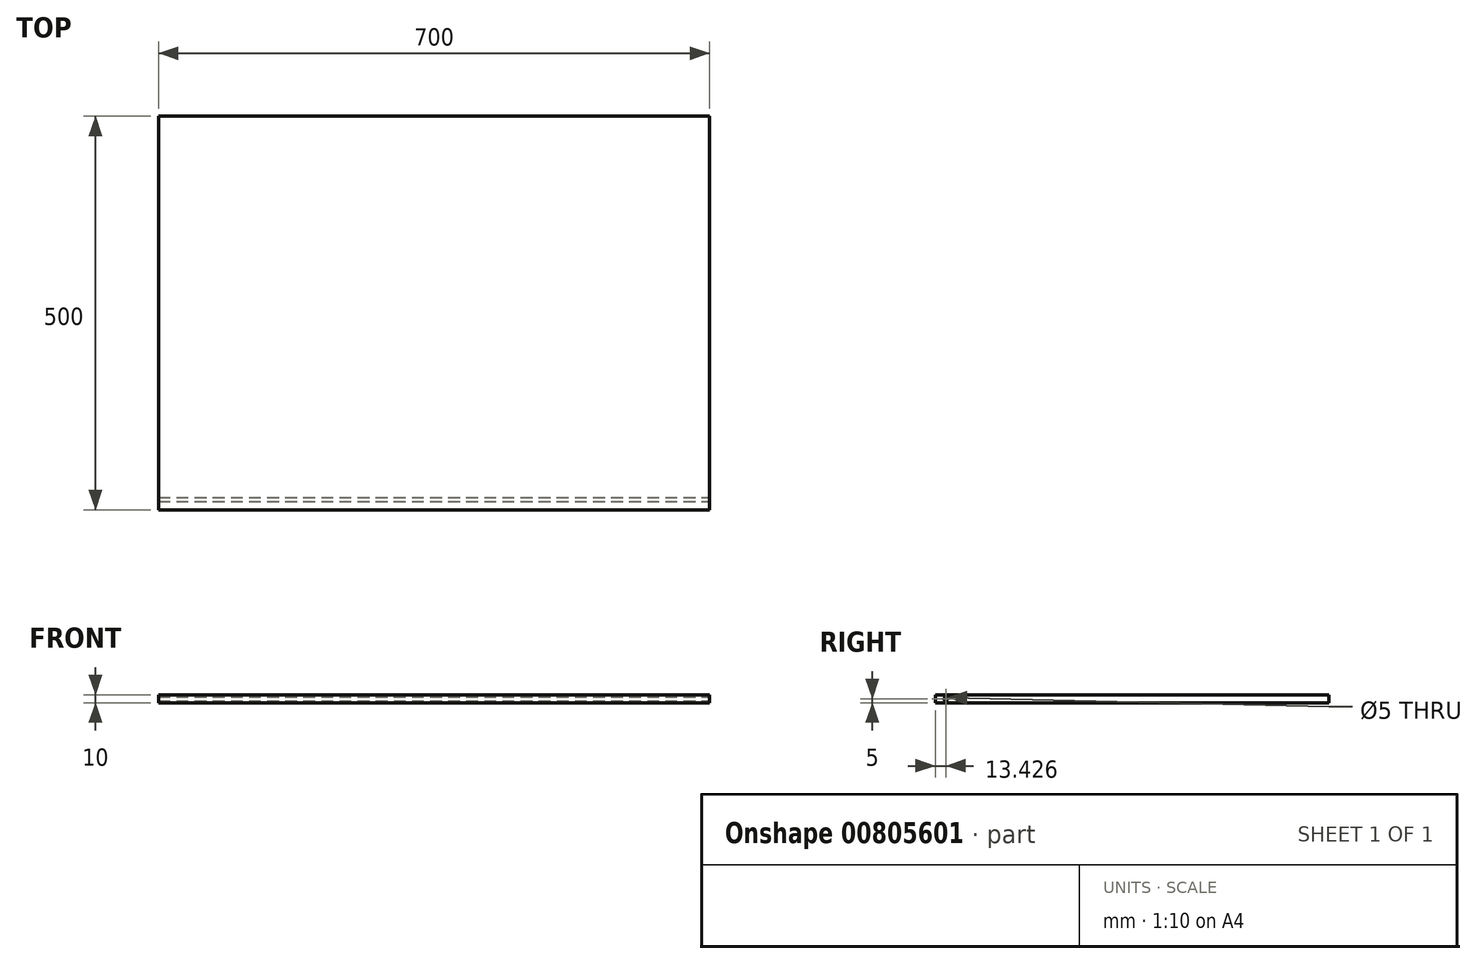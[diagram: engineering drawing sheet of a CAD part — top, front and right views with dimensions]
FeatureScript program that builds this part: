
annotation { "Feature Type Name" : "Feature", "Feature Type Description" : "" }
export const myFeature = defineFeature(function(context is Context, id is Id, definition is map)
    precondition{}
    {
        {
            var Q0;
            Q0=qCreatedBy(makeId("Top.planeOp"),FACE);
            var sketch = newSketch(context, id + "F0", { "sketchPlane" : qUnion([Q0])});
            skLineSegment(sketch, "E0.bottom", {"start": v(-346.8, 224.54) * mm, "end": v(353.2, 224.54) * mm});
            skLineSegment(sketch, "E0.top", {"start": v(-346.8, -275.46) * mm, "end": v(353.2, -275.46) * mm});
            skLineSegment(sketch, "E0.left", {"start": v(-346.8, 224.54) * mm, "end": v(-346.8, -275.46) * mm});
            skLineSegment(sketch, "E0.right", {"start": v(353.2, 224.54) * mm, "end": v(353.2, -275.46) * mm});
            skSolve(sketch);
        }
        {
            var Q0;
            Q0 = qSketchRegion(id + "F0", true);
            extrude(context, id + "F1", {"entities" : qUnion([Q0]), "depth" : 10 * mm, "offsetDistance" : 25 * mm});
        }
        {
            var Q0;
            Q0=makeQuery(id+"F1.opExtrude","SWEPT_FACE",FACE,{"disambiguationData":[OSD([sQuery(id+"F0.wireOp",EDGE,"E0.right")])]});
            var sketch = newSketch(context, id + "F2", { "sketchPlane" : qUnion([Q0])});
            skCircle(sketch, "E1", {"center": v(-266.18, 5.85) * mm, "radius": 4.15 * mm});
            skSolve(sketch);
        }
        {
            var Q0;
            Q0 = qSketchRegion(id + "F2", true);
            extrude(context, id + "F3", {"entities" : qUnion([Q0]), "operationType" : NewBodyOperationType.ADD, "oppositeDirection" : true, "depth" : 700 * mm, "offsetDistance" : 25 * mm});
        }
        {
            var Q0;
            Q0=makeQuery(id+"F1.opExtrude","SWEPT_FACE",FACE,{"disambiguationData":[OSD([sQuery(id+"F0.wireOp",EDGE,"E0.right")])]});
            var sketch = newSketch(context, id + "F4", { "sketchPlane" : qUnion([Q0])});
            skCircle(sketch, "E2", {"center": v(-262.03, 5) * mm, "radius": 3.78 * mm});
            skPoint(sketch, "E2.centerSnap0", {"position": v(-275.46, 5) * mm});
            skSolve(sketch);
        }
        {
            var Q0;
            Q0=sQuery(id+"F4.wireOp",VERTEX,"E2.center");
            var Q1;
            Q1=makeQuery(id+"F1.opExtrude","SWEPT_BODY",BODY,{"disambiguationData":[OSD([sQuery(id+"F0.wireOp",EDGE,"E0.bottom"),sQuery(id+"F0.wireOp",EDGE,"E0.top"),sQuery(id+"F0.wireOp",EDGE,"E0.left"),sQuery(id+"F0.wireOp",EDGE,"E0.right")])]});
            hole(context, id + "F5", {"style" : HoleStyle.SIMPLE, "endStyle" : HoleEndStyle.THROUGH, "holeDiameter" : 5 * mm, "majorDiameter" : 5 * mm, "isTappedThrough" : true, "tappedDepth" : 12 * mm, "tapClearance" : 3, "locations" : qUnion([Q0]), "scope" : qUnion([Q1])});
        }
    });
